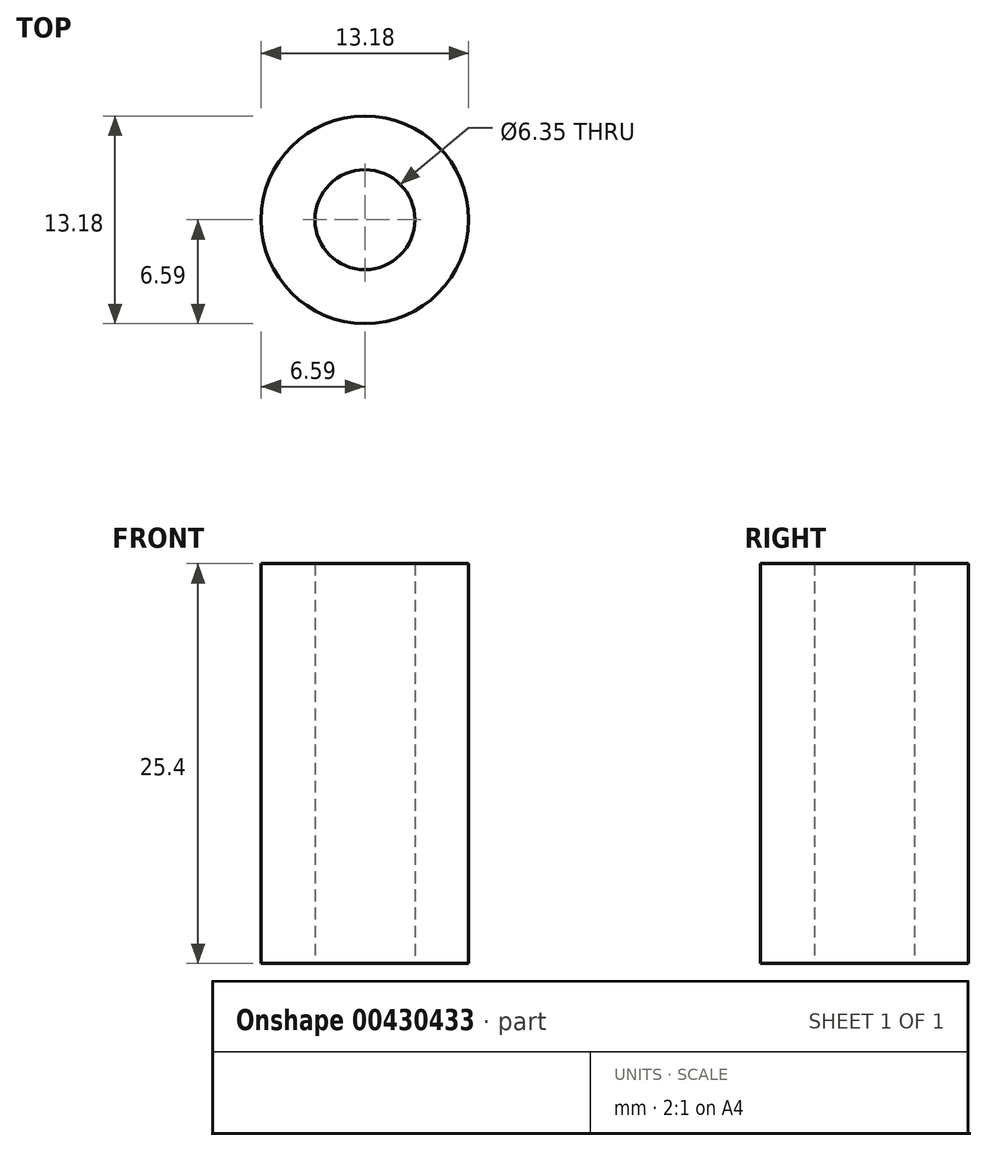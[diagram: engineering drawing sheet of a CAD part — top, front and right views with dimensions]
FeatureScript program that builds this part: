
annotation { "Feature Type Name" : "Feature", "Feature Type Description" : "" }
export const myFeature = defineFeature(function(context is Context, id is Id, definition is map)
    precondition{}
    {
        {
            var Q0;
            Q0=qCreatedBy(makeId("Top.planeOp"),FACE);
            var sketch = newSketch(context, id + "F0", { "sketchPlane" : qUnion([Q0])});
            skCircle(sketch, "E0", {"center": v(0, 0) * mm, "radius": 3.18 * mm});
            skCircle(sketch, "E1", {"center": v(0, 0) * mm, "radius": 6.59 * mm});
            skSolve(sketch);
        }
        {
            var Q0;
            Q0 = qSketchRegion(id + "F0", true);
            extrude(context, id + "F1", {"entities" : qUnion([Q0]), "depth" : 25.4 * mm});
        }
    });
